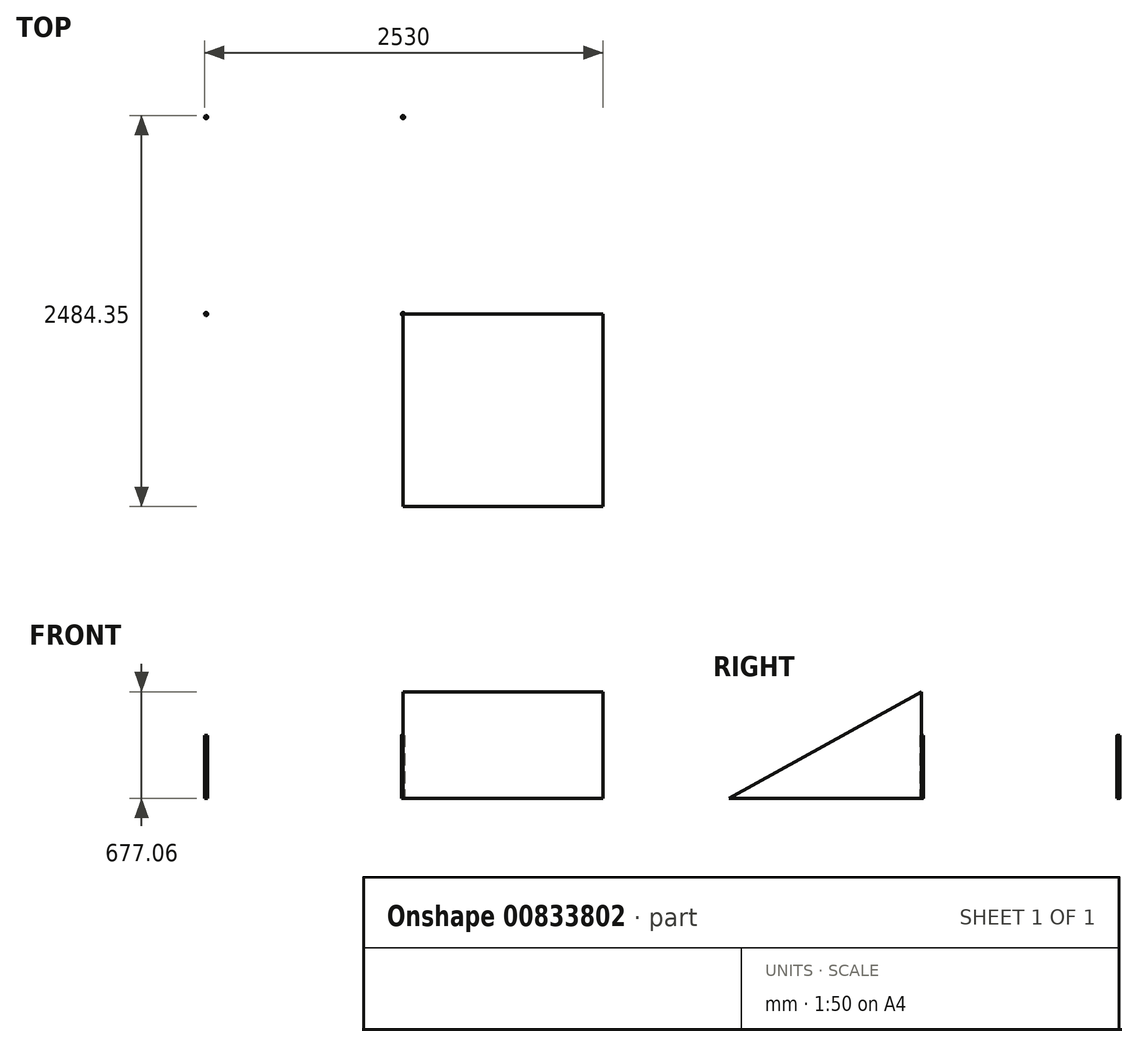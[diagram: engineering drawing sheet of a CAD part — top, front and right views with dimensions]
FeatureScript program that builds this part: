
annotation { "Feature Type Name" : "Feature", "Feature Type Description" : "" }
export const myFeature = defineFeature(function(context is Context, id is Id, definition is map)
    precondition{}
    {
        {
            var Q0;
            Q0=qCreatedBy(makeId("Top.planeOp"),FACE);
            var sketch = newSketch(context, id + "F0", { "sketchPlane" : qUnion([Q0])});
            skLineSegment(sketch, "E0", {"start": v(0, 0) * mm, "end": v(0, 1250) * mm});
            skLineSegment(sketch, "E1", {"start": v(0, 1250) * mm, "end": v(-1250, 1250) * mm});
            skLineSegment(sketch, "E2", {"start": v(-1250, 1250) * mm, "end": v(-1250, 0) * mm});
            skLineSegment(sketch, "E3", {"start": v(-1250, 0) * mm, "end": v(0, 0) * mm});
            skCircle(sketch, "E4", {"center": v(-1250, 1250) * mm, "radius": 10 * mm});
            skCircle(sketch, "E5", {"center": v(-1250, 0) * mm, "radius": 10 * mm});
            skCircle(sketch, "E6", {"center": v(0, 1250) * mm, "radius": 10 * mm});
            skCircle(sketch, "E7", {"center": v(0, 0) * mm, "radius": 10 * mm});
            skSolve(sketch);
        }
        {
            var Q0;
            {var subQ0=sQuery(id+"F0.wireOp",EDGE,"E1");var subQ1=sQuery(id+"F0.wireOp",EDGE,"E0");var subQ2=makeQuery(id+"F0.imprint","INTERSECT",VERTEX,{"derivedFrom":[subQ1,subQ0]});Q0=makeQuery(id+"F0.imprint","IMPRINT",FACE,{"disambiguationData":[TD([[makeQuery(id+"F0.imprint","IMPRINT",EDGE,{"disambiguationData":[TD([[subQ2,1.0]])],"derivedFrom":subQ1}),-1.0]])]});}
            var Q1;
            {var subQ0=sQuery(id+"F0.wireOp",EDGE,"E1");var subQ1=sQuery(id+"F0.wireOp",EDGE,"E0");var subQ2=makeQuery(id+"F0.imprint","INTERSECT",VERTEX,{"derivedFrom":[subQ1,subQ0]});Q1=makeQuery(id+"F0.imprint","IMPRINT",FACE,{"disambiguationData":[TD([[makeQuery(id+"F0.imprint","IMPRINT",EDGE,{"disambiguationData":[TD([[subQ2,1.0]])],"derivedFrom":subQ1}),1.0]])]});}
            var Q2;
            {var subQ0=sQuery(id+"F0.wireOp",EDGE,"E2");var subQ1=sQuery(id+"F0.wireOp",EDGE,"E1");var subQ2=makeQuery(id+"F0.imprint","INTERSECT",VERTEX,{"derivedFrom":[subQ1,subQ0]});Q2=makeQuery(id+"F0.imprint","IMPRINT",FACE,{"disambiguationData":[TD([[makeQuery(id+"F0.imprint","IMPRINT",EDGE,{"disambiguationData":[TD([[subQ2,1.0]])],"derivedFrom":subQ1}),-1.0]])]});}
            var Q3;
            {var subQ0=sQuery(id+"F0.wireOp",EDGE,"E2");var subQ1=sQuery(id+"F0.wireOp",EDGE,"E1");var subQ2=makeQuery(id+"F0.imprint","INTERSECT",VERTEX,{"derivedFrom":[subQ1,subQ0]});Q3=makeQuery(id+"F0.imprint","IMPRINT",FACE,{"disambiguationData":[TD([[makeQuery(id+"F0.imprint","IMPRINT",EDGE,{"disambiguationData":[TD([[subQ2,1.0]])],"derivedFrom":subQ1}),1.0]])]});}
            var Q4;
            {var subQ0=sQuery(id+"F0.wireOp",EDGE,"E3");var subQ1=sQuery(id+"F0.wireOp",EDGE,"E2");var subQ2=makeQuery(id+"F0.imprint","INTERSECT",VERTEX,{"derivedFrom":[subQ1,subQ0]});Q4=makeQuery(id+"F0.imprint","IMPRINT",FACE,{"disambiguationData":[TD([[makeQuery(id+"F0.imprint","IMPRINT",EDGE,{"disambiguationData":[TD([[subQ2,1.0]])],"derivedFrom":subQ1}),-1.0]])]});}
            var Q5;
            {var subQ0=sQuery(id+"F0.wireOp",EDGE,"E3");var subQ1=sQuery(id+"F0.wireOp",EDGE,"E2");var subQ2=makeQuery(id+"F0.imprint","INTERSECT",VERTEX,{"derivedFrom":[subQ1,subQ0]});Q5=makeQuery(id+"F0.imprint","IMPRINT",FACE,{"disambiguationData":[TD([[makeQuery(id+"F0.imprint","IMPRINT",EDGE,{"disambiguationData":[TD([[subQ2,1.0]])],"derivedFrom":subQ1}),1.0]])]});}
            var Q6;
            {var subQ0=sQuery(id+"F0.wireOp",EDGE,"E3");var subQ1=sQuery(id+"F0.wireOp",EDGE,"E0");var subQ2=makeQuery(id+"F0.imprint","INTERSECT",VERTEX,{"derivedFrom":[subQ1,subQ0]});Q6=makeQuery(id+"F0.imprint","IMPRINT",FACE,{"disambiguationData":[TD([[makeQuery(id+"F0.imprint","IMPRINT",EDGE,{"disambiguationData":[TD([[subQ2,-1.0]])],"derivedFrom":subQ1}),-1.0]])]});}
            var Q7;
            {var subQ0=sQuery(id+"F0.wireOp",EDGE,"E3");var subQ1=sQuery(id+"F0.wireOp",EDGE,"E0");var subQ2=makeQuery(id+"F0.imprint","INTERSECT",VERTEX,{"derivedFrom":[subQ1,subQ0]});Q7=makeQuery(id+"F0.imprint","IMPRINT",FACE,{"disambiguationData":[TD([[makeQuery(id+"F0.imprint","IMPRINT",EDGE,{"disambiguationData":[TD([[subQ2,-1.0]])],"derivedFrom":subQ1}),1.0]])]});}
            extrude(context, id + "F1", {"entities" : qUnion([Q0, Q1, Q2, Q3, Q4, Q5, Q6, Q7]), "depth" : 400 * mm, "offsetDistance" : 25 * mm});
        }
        {
            var Q0;
            Q0=qCreatedBy(makeId("Front.planeOp"),FACE);
            var sketch = newSketch(context, id + "F2", { "sketchPlane" : qUnion([Q0])});
            skLineSegment(sketch, "E8", {"start": v(0, 0) * mm, "end": v(1224.35, 0) * mm});
            skLineSegment(sketch, "E9", {"start": v(0, 400.34) * mm, "end": v(0, 0) * mm});
            skLineSegment(sketch, "E10", {"start": v(0, 641.1) * mm, "end": v(0, 0) * mm});
            skLineSegment(sketch, "E11", {"start": v(1224.35, 0) * mm, "end": v(0, 677.06) * mm});
            skLineSegment(sketch, "E12", {"start": v(0, 677.06) * mm, "end": v(0, 0) * mm});
            skSolve(sketch);
        }
        {
            var Q0;
            Q0=makeQuery(id+"F2.imprint","IMPRINT",FACE,{"disambiguationData":[TD([[makeQuery(id+"F2.imprint","IMPRINT",EDGE,{"derivedFrom":sQuery(id+"F2.wireOp",EDGE,"E8")}),1.0]])]});
            extrude(context, id + "F3", {"entities" : qUnion([Q0]), "oppositeDirection" : true, "depth" : 1270 * mm, "offsetDistance" : 25 * mm});
        }
        {
            var Q0;
            Q0=makeQuery(id+"F3.opExtrude","SWEPT_BODY",BODY,{"disambiguationData":[OSD([sQuery(id+"F2.wireOp",EDGE,"E8"),sQuery(id+"F2.wireOp",EDGE,"E11"),sQuery(id+"F2.wireOp",EDGE,"E12")])]});
            var Q1;
            Q1=makeQuery(id+"F1.opExtrude","SWEPT_FACE",FACE,{"disambiguationData":[OSD([sQuery(id+"F0.wireOp",EDGE,"E7")])]});
            transform(context, id + "F4", {"entities" : qUnion([Q0]), "transformType" : TransformType.ROTATION, "transformAxis" : qUnion([Q1]), "angle" : 90 * degree, "makeCopy" : false});
        }
    });
